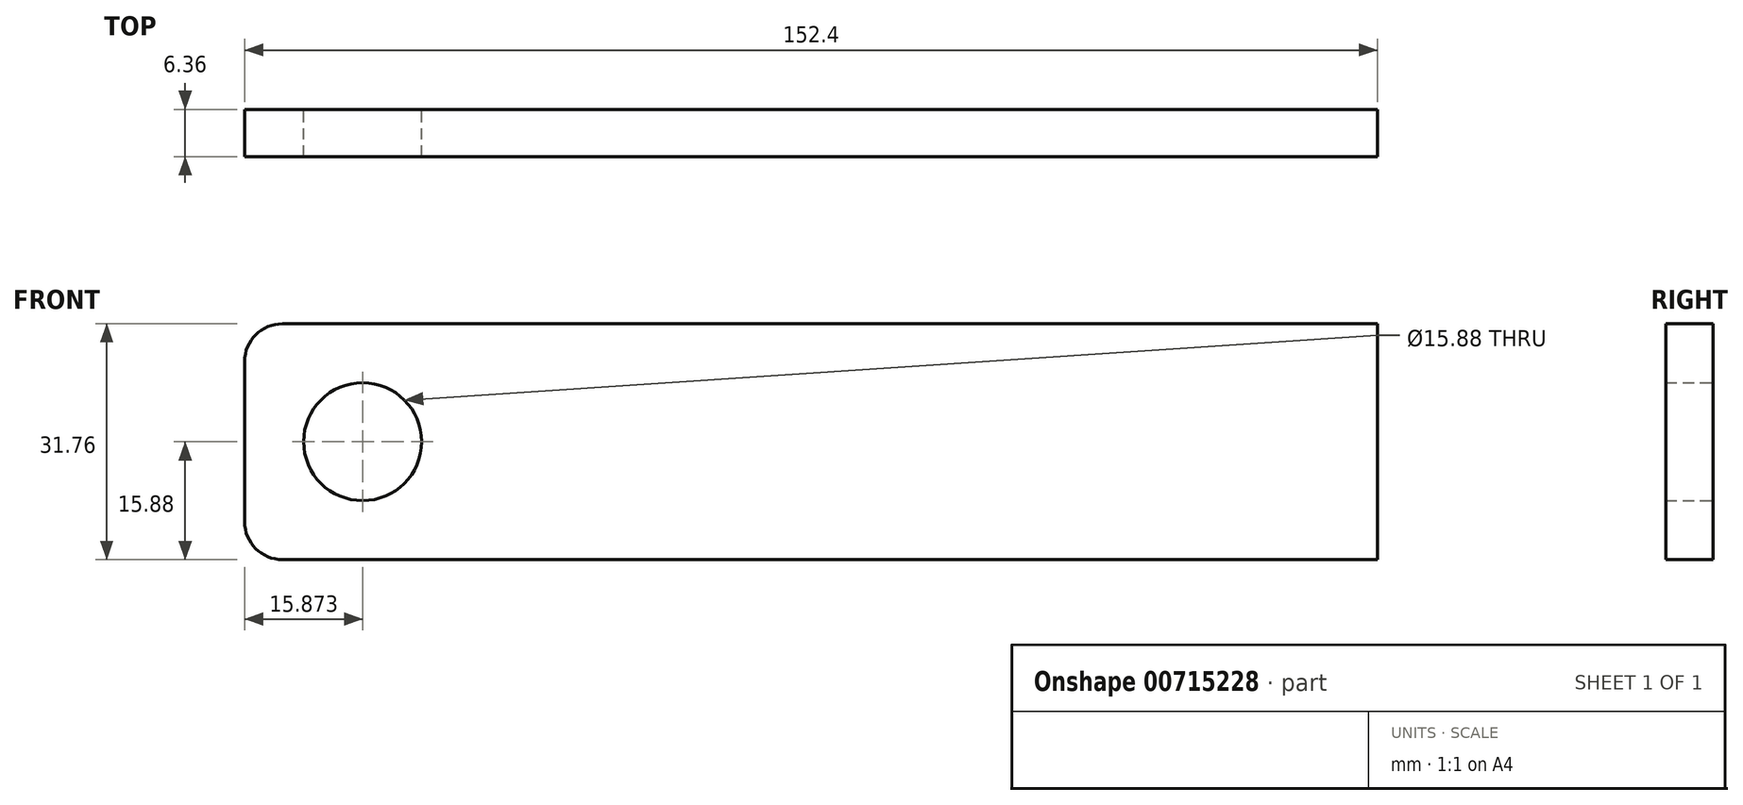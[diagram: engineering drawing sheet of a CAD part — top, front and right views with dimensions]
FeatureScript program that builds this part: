
annotation { "Feature Type Name" : "Feature", "Feature Type Description" : "" }
export const myFeature = defineFeature(function(context is Context, id is Id, definition is map)
    precondition{}
    {
        {
            var Q0;
            Q0=qCreatedBy(makeId("Front.planeOp"),FACE);
            var sketch = newSketch(context, id + "F0", { "sketchPlane" : qUnion([Q0])});
            skLineSegment(sketch, "E0.bottom", {"start": v(78.5, -15.87) * mm, "end": v(-73.9, -15.88) * mm});
            skLineSegment(sketch, "E0.top", {"start": v(78.5, 15.88) * mm, "end": v(-73.9, 15.87) * mm});
            skLineSegment(sketch, "E0.left", {"start": v(78.5, -15.87) * mm, "end": v(78.5, 15.88) * mm});
            skLineSegment(sketch, "E0.right", {"start": v(-73.9, -15.88) * mm, "end": v(-73.9, 15.87) * mm});
            skPoint(sketch, "E0.middle", {"position": v(2.3, 0) * mm});
            skCircle(sketch, "E1", {"center": v(-58.03, 0) * mm, "radius": 7.94 * mm});
            skPoint(sketch, "E1.centerSnap0", {"position": v(-73.9, 0) * mm});
            skSolve(sketch);
        }
        {
            var Q0;
            Q0 = qSketchRegion(id + "F0", true);
            extrude(context, id + "F1", {"entities" : qUnion([Q0]), "endBound" : BoundingType.SYMMETRIC, "depth" : 6.35 * mm, "offsetDistance" : 25.4 * mm});
        }
        {
            var Q0;
            Q0=makeQuery(id+"F1.opExtrude","SWEPT_EDGE",EDGE,{"disambiguationData":[OSD([sQuery(id+"F0.wireOp",EDGE,"E0.top"),sQuery(id+"F0.wireOp",EDGE,"E0.right")])]});
            var Q1;
            Q1=makeQuery(id+"F1.opExtrude","SWEPT_EDGE",EDGE,{"disambiguationData":[OSD([sQuery(id+"F0.wireOp",EDGE,"E0.bottom"),sQuery(id+"F0.wireOp",EDGE,"E0.right")])]});
            fillet(context, id + "F2", {"entities" : qUnion([Q0, Q1]), "radius" : 5.08 * mm, "tangentPropagation" : true, "allowEdgeOverflow" : false});
        }
    });
